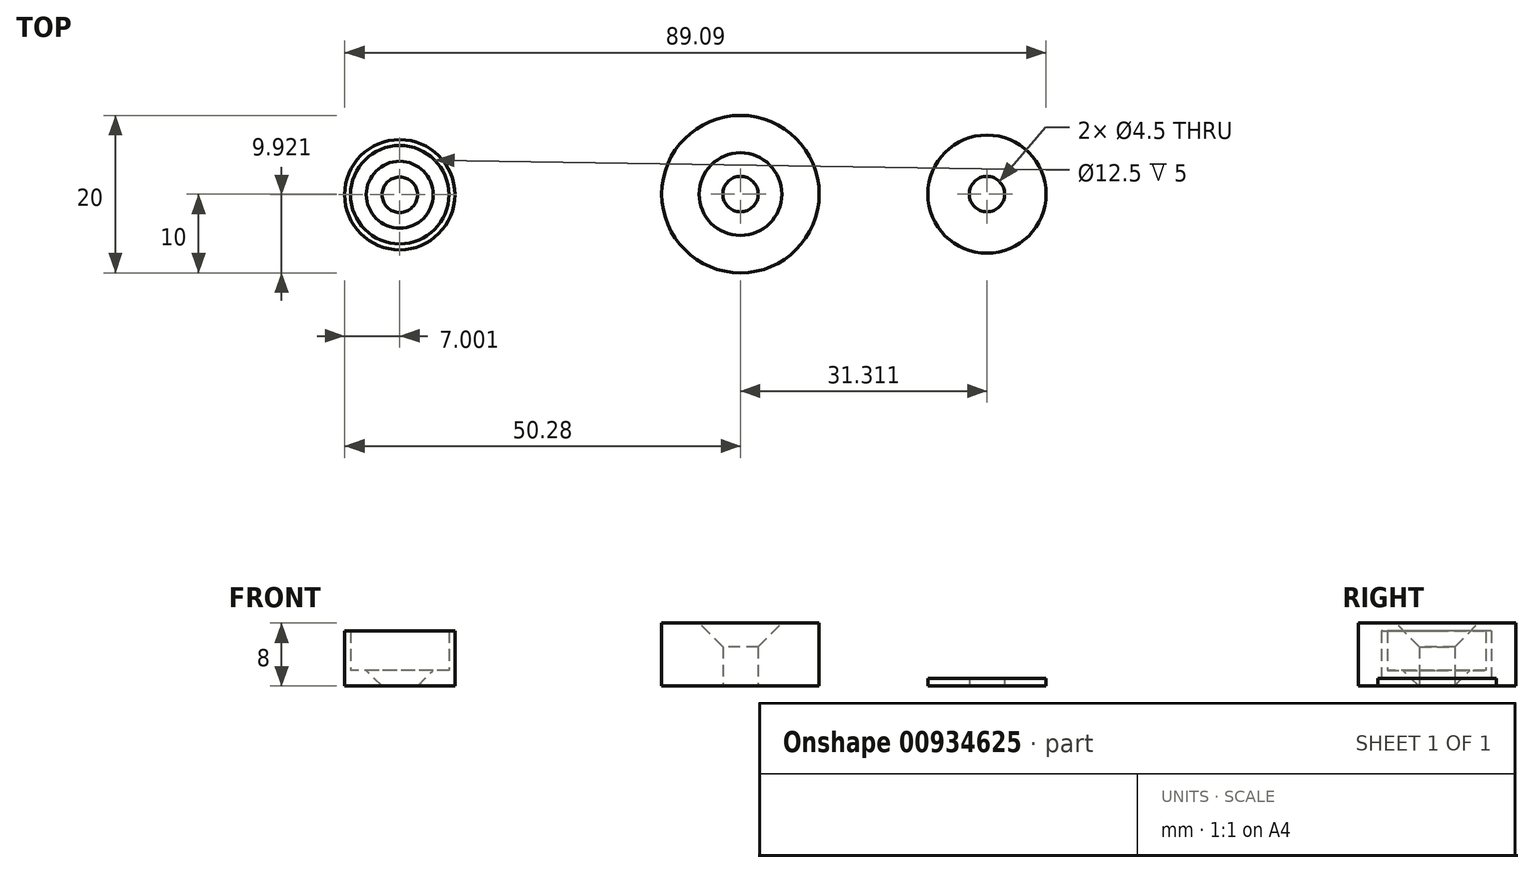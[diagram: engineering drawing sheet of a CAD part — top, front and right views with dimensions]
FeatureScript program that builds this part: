
annotation { "Feature Type Name" : "Feature", "Feature Type Description" : "" }
export const myFeature = defineFeature(function(context is Context, id is Id, definition is map)
    precondition{}
    {
        {
            var Q0;
            Q0=qCreatedBy(makeId("Top.planeOp"),FACE);
            var sketch = newSketch(context, id + "F0", { "sketchPlane" : qUnion([Q0])});
            skCircle(sketch, "E0", {"center": v(0, 0) * mm, "radius": 10 * mm});
            skCircle(sketch, "E1", {"center": v(0, 0) * mm, "radius": 2.25 * mm});
            skCircle(sketch, "E2", {"center": v(31.31, 0) * mm, "radius": 7.5 * mm});
            skCircle(sketch, "E3", {"center": v(31.31, 0) * mm, "radius": 2.25 * mm});
            skCircle(sketch, "E4", {"center": v(-43.28, -0.08) * mm, "radius": 7 * mm});
            skCircle(sketch, "E5", {"center": v(-43.28, -0.08) * mm, "radius": 6.25 * mm});
            skCircle(sketch, "E6", {"center": v(-43.28, -0.08) * mm, "radius": 2.25 * mm});
            skSolve(sketch);
        }
        {
            var Q0;
            Q0=makeQuery(id+"F0.imprint","IMPRINT",FACE,{"disambiguationData":[TD([[makeQuery(id+"F0.imprint","IMPRINT",EDGE,{"derivedFrom":sQuery(id+"F0.wireOp",EDGE,"E0")}),1.0]])]});
            extrude(context, id + "F1", {"entities" : qUnion([Q0]), "depth" : 8 * mm, "offsetDistance" : 25 * mm});
        }
        {
            var Q0;
            Q0=makeQuery(id+"F1.opExtrude","CAP_EDGE",EDGE,{"disambiguationData":[OSD([sQuery(id+"F0.wireOp",EDGE,"E1")])],"isStart":false});
            chamfer(context, id + "F2", {"entities" : qUnion([Q0]), "width" : 3 * mm, "tangentPropagation" : true});
        }
        {
            var Q0;
            Q0=makeQuery(id+"F0.imprint","IMPRINT",FACE,{"disambiguationData":[TD([[makeQuery(id+"F0.imprint","IMPRINT",EDGE,{"derivedFrom":sQuery(id+"F0.wireOp",EDGE,"E2")}),1.0]])]});
            extrude(context, id + "F3", {"entities" : qUnion([Q0]), "depth" : 1 * mm, "offsetDistance" : 25 * mm});
        }
        {
            var Q0;
            Q0=makeQuery(id+"F0.imprint","IMPRINT",FACE,{"disambiguationData":[TD([[makeQuery(id+"F0.imprint","IMPRINT",EDGE,{"derivedFrom":sQuery(id+"F0.wireOp",EDGE,"E5")}),1.0]])]});
            var Q1;
            Q1=makeQuery(id+"F0.imprint","IMPRINT",FACE,{"disambiguationData":[TD([[makeQuery(id+"F0.imprint","IMPRINT",EDGE,{"derivedFrom":sQuery(id+"F0.wireOp",EDGE,"E4")}),1.0]])]});
            extrude(context, id + "F4", {"entities" : qUnion([Q0, Q1]), "depth" : 2 * mm, "offsetDistance" : 25 * mm});
        }
        {
            var Q0;
            Q0=makeQuery(id+"F0.imprint","IMPRINT",FACE,{"disambiguationData":[TD([[makeQuery(id+"F0.imprint","IMPRINT",EDGE,{"derivedFrom":sQuery(id+"F0.wireOp",EDGE,"E4")}),1.0]])]});
            extrude(context, id + "F5", {"entities" : qUnion([Q0]), "operationType" : NewBodyOperationType.ADD, "depth" : 7 * mm, "offsetDistance" : 25 * mm});
        }
        {
            var Q0;
            Q0=makeQuery(id+"F4.opExtrude","CAP_EDGE",EDGE,{"disambiguationData":[OSD([sQuery(id+"F0.wireOp",EDGE,"E6")])],"isStart":false});
            chamfer(context, id + "F6", {"entities" : qUnion([Q0]), "width" : 2 * mm, "tangentPropagation" : true});
        }
    });
